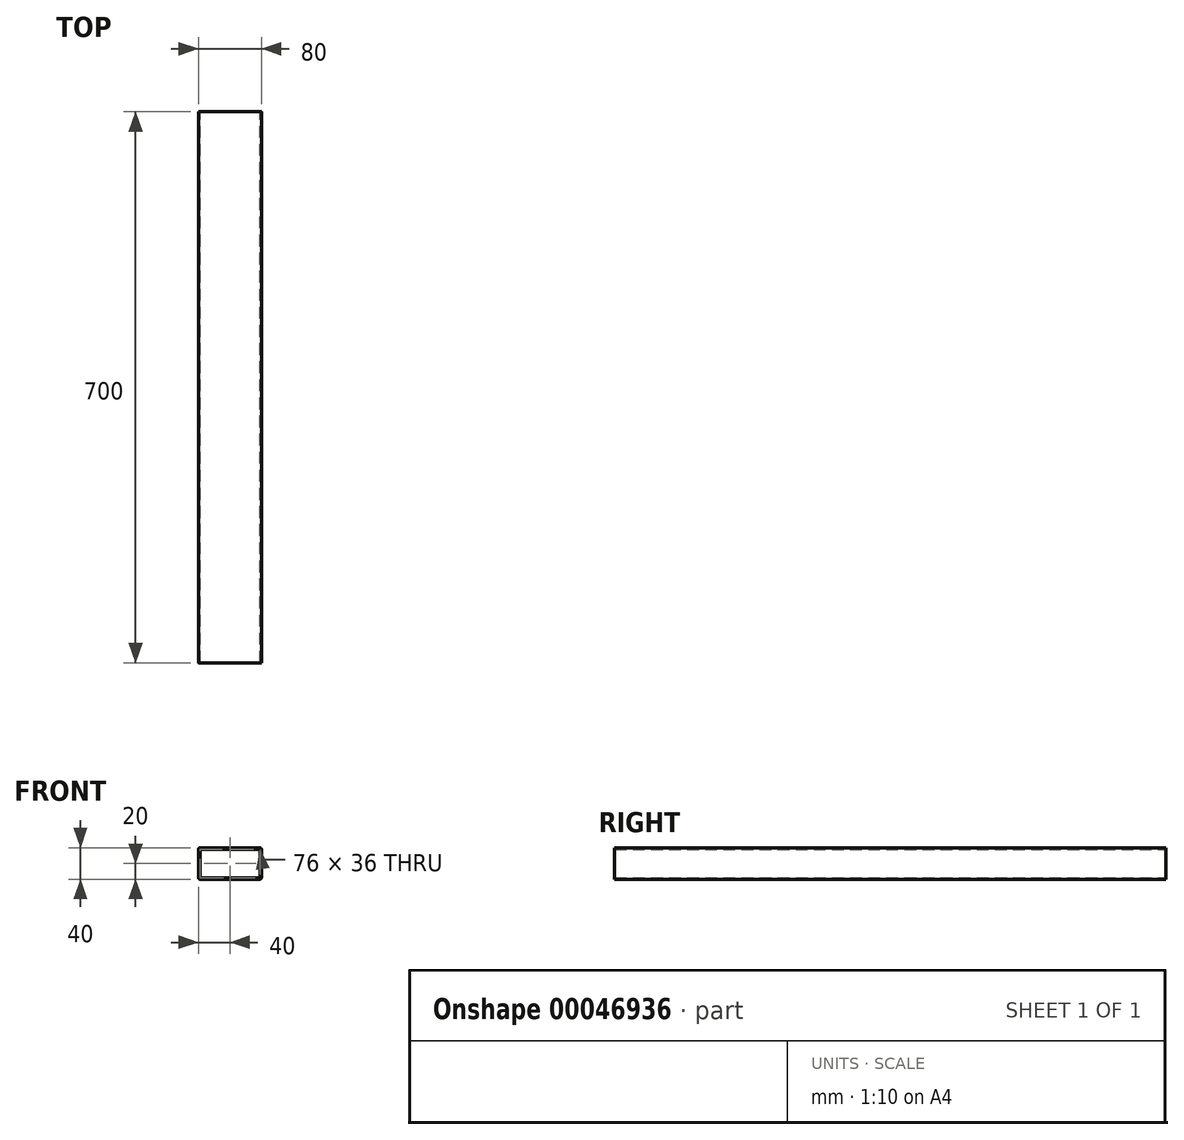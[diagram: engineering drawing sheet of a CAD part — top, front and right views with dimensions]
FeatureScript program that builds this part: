
annotation { "Feature Type Name" : "Feature", "Feature Type Description" : "" }
export const myFeature = defineFeature(function(context is Context, id is Id, definition is map)
    precondition{}
    {
        {
            var Q0;
            Q0=qCreatedBy(makeId("Front.planeOp"),FACE);
            var sketch = newSketch(context, id + "F0", { "sketchPlane" : qUnion([Q0])});
            skLineSegment(sketch, "E0", {"start": v(38, 18) * mm, "end": v(38, -18) * mm});
            skLineSegment(sketch, "E1", {"start": v(-38, 18) * mm, "end": v(38, 18) * mm});
            skLineSegment(sketch, "E2", {"start": v(-38, -18) * mm, "end": v(-38, 18) * mm});
            skLineSegment(sketch, "E3", {"start": v(38, -18) * mm, "end": v(-38, -18) * mm});
            skLineSegment(sketch, "E4", {"start": v(-40, 18) * mm, "end": v(-40, -18) * mm});
            skArc(sketch, "E5", {"start": v(-38, 20) * mm, "mid": v(-39.41, 19.41) * mm, "end": v(-40, 18) * mm});
            skLineSegment(sketch, "E6", {"start": v(38, 20) * mm, "end": v(-38, 20) * mm});
            skArc(sketch, "E7", {"start": v(40, 18) * mm, "mid": v(39.41, 19.41) * mm, "end": v(38, 20) * mm});
            skLineSegment(sketch, "E8", {"start": v(40, -18) * mm, "end": v(40, 18) * mm});
            skArc(sketch, "E9", {"start": v(38, -20) * mm, "mid": v(39.41, -19.41) * mm, "end": v(40, -18) * mm});
            skLineSegment(sketch, "E10", {"start": v(-38, -20) * mm, "end": v(38, -20) * mm});
            skArc(sketch, "E11", {"start": v(-40, -18) * mm, "mid": v(-39.41, -19.41) * mm, "end": v(-38, -20) * mm});
            skSolve(sketch);
        }
        {
            var Q0;
            Q0=qSketchRegion(id+"F0",true);
            extrude(context, id + "F1", {"entities" : qUnion([Q0]), "depth" : 700 * mm});
        }
    });
